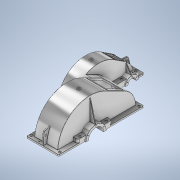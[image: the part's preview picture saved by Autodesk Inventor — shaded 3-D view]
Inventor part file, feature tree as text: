
AUTODESK INVENTOR PART (.ipt)
format: ipt  version: 2020 (Build 240168000, 168)  size: 2,549,760 bytes
history: native  units: mm
features: sketch x87, extrude x70, projected_geometry x45, plane x34, other x25, hole x17, mirror x14, fillet x14, reference x7
ambient origin geometry x8: Origin, YZ Plane, XZ Plane, XY Plane, X Axis, Y Axis, Z Axis, Center Point
bodies: 实体1 (feature_tree), 实体2 (feature_tree)
feature tree (313):
  plane  "工作平面1"
  extrude  "拉伸1"  Depth=10.0mm TaperAngle=0.0deg
  plane  "工作平面2"
  extrude  "拉伸2"  Depth=10.0mm TaperAngle=0.0deg
  plane  "工作平面3"
  extrude  "拉伸3"  Depth=10.0mm TaperAngle=0.0deg
  plane  "工作平面4"
  extrude  "拉伸4"  Depth=15.0mm TaperAngle=0.0deg
  plane  "工作平面5"
  extrude  "拉伸5"  [1 undecoded]
  sketch  "草图7"  dims[d52=10.0mm d53=0.0mm d54=10.0mm d55=0.0mm]
  plane  "工作平面6"
  extrude  "拉伸6"  Depth=10.0mm
  plane  "工作平面7"
  extrude  "拉伸7"  Depth=15.0mm
  extrude  "拉伸8"  Depth=10.0mm TaperAngle=0.0deg
  plane  "工作平面8"
  sketch  "草图11"  dims[d56=8.0mm d57=0.0mm d58=15.0mm d59=0.0mm]
  sketch  "草图12"  dims[d60=15.0mm d61=0.0mm d62=-10.0mm]
  extrude  "拉伸9"  [1 undecoded]
  extrude  "拉伸10"  Depth=10.0mm
  other  "对称面1"
  mirror  "镜像1"
  extrude  "拉伸11"  Depth=10.0mm TaperAngle=0.0deg
  sketch  "草图15"  dims[d74=15.0mm d75=0.0mm d76=10.0mm d77=0.0mm]
  other  "工作面101"
  sketch  "草图16"  dims[d78=10.0mm d79=0.0mm d80=-10.0mm]
  plane  "工作平面11"
  extrude  "拉伸12"  Depth=143.0mm TaperAngle=0.0deg
  other  "对称面2"
  extrude  "拉伸13"  Depth=10.0mm TaperAngle=0.0deg
  extrude  "拉伸14"  Depth=10.0mm TaperAngle=0.0deg
  fillet  "圆角2"  Radius=10.0mm
  extrude  "拉伸15"  Depth=10.0mm TaperAngle=0.0deg
  extrude  "拉伸16"  Depth=36.0mm
  mirror  "镜像2"
  extrude  "拉伸17"  Depth=35.0mm
  plane  "工作平面13"
  extrude  "拉伸18"  Depth=10.0mm TaperAngle=0.0deg
  plane  "工作平面14"
  extrude  "拉伸19"  Depth=10.0mm TaperAngle=0.0deg
  plane  "工作平面15"
  extrude  "拉伸20"  Depth=10.0mm TaperAngle=0.0deg
  other  "合并1"
  extrude  "拉伸21"  Depth=8.0mm TaperAngle=0.0deg
  mirror  "镜像3"
  extrude  "拉伸22"  Depth=5.0mm TaperAngle=0.0deg
  mirror  "镜像4"
  plane  "工作平面16"
  extrude  "拉伸23"  Depth=5.0mm TaperAngle=0.0deg
  extrude  "拉伸24"  Depth=36.0mm
  extrude  "拉伸25"  Depth=50.0mm
  sketch  "草图34"  dims[d131=5.0mm d132=0.0mm d133=5.0mm d134=0.0mm]
  extrude  "拉伸26"  Depth=7.0mm TaperAngle=0.0deg
  extrude  "拉伸27"  Depth=10.0mm TaperAngle=0.0deg
  sketch  "草图36"  dims[d138=5.0mm d139=0.0mm d140=50.0mm]
  extrude  "拉伸28"  Depth=70.0mm
  extrude  "拉伸29"  Depth=15.0mm TaperAngle=0.0deg
  extrude  "拉伸30"  Depth=23.0mm
  extrude  "拉伸31"  Depth=10.0mm TaperAngle=0.0deg
  extrude  "拉伸32"  Depth=36.0mm
  extrude  "拉伸33"  Depth=10.0mm TaperAngle=0.0deg
  extrude  "拉伸34"  Depth=10.0mm TaperAngle=0.0deg
  extrude  "拉伸35"  Depth=46.0mm TaperAngle=0.0deg
  extrude  "拉伸36"  Depth=12.0mm
  extrude  "拉伸37"  Depth=100.0mm
  other  "对称面4"
  mirror  "镜像5"
  extrude  "拉伸38"  Depth=46.0mm TaperAngle=0.0deg
  sketch  "草图48"  dims[d178=20.0mm d179=100.0mm]
  extrude  "拉伸39"  Depth=10.0mm TaperAngle=0.0deg
  extrude  "拉伸40"  Depth=10.0mm TaperAngle=0.0deg
  extrude  "拉伸41"  Depth=10.0mm
  extrude  "拉伸42"  [1 undecoded]
  extrude  "拉伸43"  [1 undecoded]
  extrude  "拉伸44"  Depth=10.0mm TaperAngle=0.0deg
  sketch  "草图53"  dims[d193=10.0mm d194=0.0mm d195=-10.0mm]
  extrude  "拉伸45"  Depth=113.0mm
  extrude  "拉伸46"  TaperAngle=0.0deg  [1 undecoded]
  extrude  "拉伸47"  Depth=206.0mm
  extrude  "拉伸48"  TaperAngle=0.0deg  [1 undecoded]
  extrude  "拉伸49"  Depth=1.0mm
  extrude  "拉伸50"  Depth=1.0mm
  other  "工作轴2"
  extrude  "拉伸51"  Depth=1.0mm
  plane  "工作平面19"
  mirror  "镜像6"
  plane  "工作平面20"
  mirror  "镜像7"
  fillet  "圆角3"  Radius=16.580628mm
  fillet  "圆角4"  Radius=19.198622mm
  sketch  "草图60"  dims[d213=180.0mm d214=0.0mm]
  extrude  "拉伸52"  Depth=1.0mm
  extrude  "拉伸53"  Depth=20.0mm
  extrude  "拉伸54"  TaperAngle=105.0deg  [1 undecoded]
  extrude  "拉伸55"  Depth=110.0mm
  extrude  "拉伸56"  Depth=20.0mm
  extrude  "拉伸57"  Depth=90.0mm
  plane  "工作平面21"
  plane  "工作平面22"
  extrude  "拉伸58"  Depth=90.0mm
  extrude  "拉伸59"  Depth=140.0mm
  extrude  "拉伸60"  Depth=4.0mm TaperAngle=0.0deg
  extrude  "拉伸61"  Depth=110.0mm
  extrude  "拉伸63"  [1 undecoded]
  plane  "工作平面23"
  plane  "工作平面24"
  plane  "工作平面25"
  other  "加强筋1"
  mirror  "镜像8"
  other  "加强筋2"
  other  "加强筋3"
  mirror  "镜像9"
  sketch  "草图77"  dims[d291=120.0mm d292=90.0mm]
  other  "加强筋5"
  fillet  "圆角6"  Radius=30.0mm
  hole  "孔2"  [1 undecoded]
  other  "第一对称面"
  sketch  "草图79"  dims[d293=130.0mm d294=140.0mm]
  other  "加强筋6"
  hole  "孔3"  [1 undecoded]
  fillet  "圆角7"  Radius=20.0mm
  other  "第二对称面"
  plane  "工作平面28"
  plane  "工作平面29"
  plane  "工作平面30"
  hole  "孔4"  [1 undecoded]
  sketch  "草图82"  dims[d316=18.0mm d317=110.0mm]
  extrude  "拉伸65"  Depth=170.0mm
  hole  "孔6"  [1 undecoded]
  plane  "工作平面32"
  extrude  "拉伸66"  Depth=100.0mm
  hole  "孔7"  [1 undecoded]
  plane  "工作平面34"
  extrude  "拉伸67"  Depth=6.0mm
  hole  "孔8"  [1 undecoded]
  extrude  "拉伸68"  Depth=35.0mm
  hole  "孔9"  [1 undecoded]
  mirror  "镜像10"
  hole  "孔10"  [1 undecoded]
  extrude  "拉伸69"  Depth=105.0mm
  extrude  "拉伸70"  TaperAngle=30.0deg  [1 undecoded]
  fillet  "圆角8"  Radius=28.0mm
  fillet  "圆角9"  Radius=28.0mm
  hole  "孔11"  [1 undecoded]
  hole  "孔12"  [1 undecoded]
  extrude  "拉伸71"  Depth=12.0mm
  extrude  "拉伸72"  Depth=2.0mm
  hole  "孔13"  [1 undecoded]
  plane  "工作平面35"
  mirror  "镜像11"
  plane  "工作平面36"
  hole  "孔14"  [1 undecoded]
  hole  "孔15"  [1 undecoded]
  mirror  "镜像12"
  hole  "孔16"  [1 undecoded]
  other  "工作轴3"
  other  "工作轴4"
  other  "工作轴5"
  plane  "工作平面39"
  sketch  "草图104"  dims[d410=60.0mm d412=360.0deg]
  hole  "孔17"  [1 undecoded]
  mirror  "镜像13"
  plane  "工作平面40"
  hole  "孔18"  [1 undecoded]
  mirror  "镜像14"
  plane  "工作平面41"
  hole  "孔19"  [1 undecoded]
  fillet  "圆角10"  Radius=0.15mm
  fillet  "圆角11"  Radius=0.25mm
  fillet  "圆角12"  Radius=0.375mm
  fillet  "圆角13"  Radius=14.3117mm
  fillet  "圆角14"  [1 undecoded]
  fillet  "圆角15"  [1 undecoded]
  fillet  "圆角16"  [1 undecoded]
  sketch  "草图2"  dims[d0=41.0mm d1=40.0mm d2=41.0mm d3=8.0mm d4=41.0mm d5=41.0mm d6=40.0mm d7=8.0mm d8=25.0mm d9=71.0mm d10=8.0mm d11=70.0mm d12=190.0mm d13=75.0mm d14=43.0mm d15=8.0mm d16=75.0mm d17=40.0mm d18=31.0mm d19=12.0mm d20=25.0mm d21=10.0mm d22=8.0mm d23=30.0mm d24=5.0mm d25=25.0mm d26=174.0mm d27=91.0mm d28=40.0mm d29=21.0mm d30=71.0mm d31=12.0mm d32=30.0mm d33=30.0mm d34=25.0mm d35=12.0mm d36=30.0mm d37=30.0mm d38=100.0mm d39=40.0mm d40=12.0mm d41=20.0mm d42=70.0mm d43=15.0mm d44=2.0mm d45=31.0mm d46=10.0mm d47=0.0mm]
  sketch  "草图6"  dims[d48=10.0mm d49=0.0mm d50=10.0mm d51=0.0mm]
  projected_geometry  "投影回路1"
  sketch  "草图13"  dims[d66=130.0mm d71=10.0mm]
  projected_geometry  "投影回路2"
  sketch  "草图14"  dims[d72=150.0mm d73=15.0mm]
  sketch  "草图17"  dims[d82=10.0mm d83=10.0mm]
  projected_geometry  "投影回路3"
  projected_geometry  "投影回路4"
  sketch  "草图18"  dims[d84=-10.0mm d85=10.0mm d86=0.0mm]
  projected_geometry  "投影回路5"
  sketch  "草图19"  dims[d87=10.0mm d88=0.0mm d90=143.0mm d91=0.0mm]
  projected_geometry  "投影回路6"
  sketch  "草图22"  dims[d92=6.0mm d93=10.0mm d94=0.0mm]
  sketch  "草图24"  dims[d95=10.0mm d96=0.0mm d97=10.0mm d98=0.0mm d99=10.0mm d100=0.0mm]
  sketch  "草图25"  dims[d101=10.0mm d102=0.0mm d103=10.0mm d104=0.0mm]
  sketch  "草图26"  dims[d105=10.0mm d106=0.0mm d107=36.0mm]
  projected_geometry  "投影回路7"
  projected_geometry  "投影回路8"
  sketch  "草图27"  dims[d108=10.0mm d109=0.0mm d110=35.0mm]
  sketch  "草图28"  dims[d111=10.0mm d112=0.0mm d113=10.0mm d114=0.0mm]
  projected_geometry  "投影回路9"
  sketch  "草图29"  dims[d115=10.0mm d116=0.0mm d117=10.0mm d118=0.0mm]
  sketch  "草图31"  dims[d119=10.0mm d120=0.0mm d121=10.0mm d122=0.0mm]
  projected_geometry  "投影回路11"
  sketch  "草图32"  dims[d123=8.0mm d124=0.0mm d125=8.0mm d126=0.0mm]
  projected_geometry  "投影回路12"
  sketch  "草图33"  dims[d127=5.0mm d128=0.0mm d129=5.0mm d130=0.0mm]
  projected_geometry  "投影回路13"
  projected_geometry  "投影回路14"
  sketch  "草图35"  dims[d135=5.0mm d136=0.0mm d137=36.0mm]
  projected_geometry  "投影回路15"
  sketch  "草图37"  dims[d141=5.0mm d142=0.0mm d143=7.0mm d144=0.0mm]
  projected_geometry  "投影回路16"
  sketch  "草图38"  dims[d145=10.0mm d146=0.0mm d147=10.0mm d148=0.0mm]
  projected_geometry  "投影回路17"
  sketch  "草图39"  dims[d149=10.0mm d150=0.0mm d151=70.0mm]
  projected_geometry  "投影回路18"
  sketch  "草图40"  dims[d152=10.0mm d153=0.0mm d154=15.0mm d155=0.0mm]
  projected_geometry  "投影回路19"
  sketch  "草图41"  dims[d156=23.0mm d157=0.0mm d158=23.0mm]
  projected_geometry  "投影回路20"
  projected_geometry  "投影回路21"
  sketch  "草图42"  dims[d159=36.0mm d160=10.0mm d161=0.0mm]
  projected_geometry  "投影回路22"
  sketch  "草图43"  dims[d162=23.0mm d163=36.0mm]
  projected_geometry  "投影回路23"
  sketch  "草图44"  dims[d164=10.0mm d165=0.0mm d166=10.0mm d167=0.0mm]
  sketch  "草图45"  dims[d168=10.0mm d169=0.0mm d170=10.0mm d171=0.0mm]
  sketch  "草图46"  dims[d172=70.0mm d173=46.0mm d174=0.0mm]
  sketch  "草图47"  dims[d175=10.0mm d176=0.0mm d177=12.0mm]
  projected_geometry  "投影回路24"
  sketch  "草图49"  dims[d180=46.0mm d181=0.0mm d182=46.0mm d183=0.0mm]
  projected_geometry  "投影回路25"
  sketch  "草图50"  dims[d184=380.0mm d185=10.0mm d186=0.0mm]
  sketch  "草图51"  dims[d187=390.0mm d188=10.0mm d189=0.0mm]
  projected_geometry  "投影回路26"
  sketch  "草图52"  dims[d190=10.0mm d191=0.0mm d192=10.0mm]
  projected_geometry  "投影回路27"
  sketch  "草图54"  dims[d196=10.0mm d197=-10.0mm]
  projected_geometry  "投影回路28"
  sketch  "草图55"  dims[d198=10.0mm d199=0.0mm d200=10.0mm d201=0.0mm]
  projected_geometry  "投影回路29"
  sketch  "草图56"  dims[d202=10.0mm d203=0.0mm d204=113.0mm]
  projected_geometry  "投影回路30"
  sketch  "草图57"  dims[d205=120.0mm d206=0.0mm]
  sketch  "草图58"  dims[d207=2.0mm d208=0.0mm d212=206.0mm]
  projected_geometry  "投影回路31"
  projected_geometry  "投影回路42"
  projected_geometry  "投影回路43"
  sketch  "草图61"  dims[d215=2.0mm d216=0.0mm d220=1.0mm]
  sketch  "草图62"  dims[d221=9.0mm d222=0.0mm d223=0.0mm d224=1.0mm d225=1.0mm d226=1.0mm]
  sketch  "草图63"  dims[d227=9.0mm d228=0.0mm d229=0.0mm d230=1.0mm d231=1.0mm d232=1.0mm]
  sketch  "草图64"  dims[d233=9.0mm d234=0.0mm d235=0.0mm d236=1.0mm d237=1.0mm d255=16.580628mm d256=19.198622mm]
  projected_geometry  "投影回路44"
  projected_geometry  "投影回路45"
  projected_geometry  "投影回路46"
  projected_geometry  "投影回路47"
  sketch  "草图65"  dims[d257=115.0mm d258=1.0mm]
  sketch  "草图66"  dims[d259=12.0mm d260=0.0mm d261=0.0mm d262=1.0mm d263=1.0mm d264=20.0mm]
  sketch  "草图67"  dims[d265=20.0mm d266=6.0mm d267=45.0mm d268=2.0mm d269=90.0deg d270=8.0mm d271=20.594885mm d272=105.0deg]
  projected_geometry  "投影回路48"
  sketch  "草图68"  dims[d273=19.198622mm d274=110.0mm]
  sketch  "草图70"  dims[d275=1.0mm]
  sketch  "草图72"  dims[d276=12.0mm d277=0.0mm d278=0.0mm d279=1.0mm d280=1.0mm]
  sketch  "草图73"  dims[d281=20.0mm d282=6.0mm d283=26.0mm d284=2.0mm d285=90.0deg d286=8.0mm d287=20.594885mm d288=20.0mm]
  sketch  "草图74"  dims[d289=70.0mm d290=90.0mm]
  projected_geometry  "投影回路52"
  projected_geometry  "投影回路53"
  projected_geometry  "投影回路54"
  sketch  "草图81"  dims[d295=13.5mm d296=6.0mm d297=26.0mm d298=2.0mm d299=90.0deg d300=8.0mm d301=20.594885mm d302=4.0mm d303=0.0mm]
  sketch  "草图83"  dims[d318=10.0mm d319=6.0mm d320=26.0mm d321=2.0mm d322=90.0deg d323=8.0mm d324=20.594885mm d325=-3.0mm d326=30.0mm]
  sketch  "草图85"  dims[d327=10.0mm d328=0.0mm]
  plane  "工作平面31"
  sketch  "草图86"  dims[d329=15.29367mm d330=36.0mm d331=18.0mm d332=2.0mm d333=90.0deg d334=47.2mm d335=0.0mm d336=-3.0mm]
  sketch  "草图87"  dims[d337=30.0mm d338=10.0mm d339=0.0mm]
  plane  "工作平面33"
  sketch  "草图88"  dims[d340=15.29367mm d341=36.0mm d342=18.0mm d343=2.0mm d344=90.0deg d345=47.2mm d346=0.0mm d347=20.0mm d348=0.0mm]
  sketch  "草图89"  dims[d349=36.001mm d350=70.0mm]
  sketch  "草图90"  dims[d351=13.5mm d352=36.0mm d353=26.0mm d354=2.0mm d355=90.0deg d356=8.0mm d357=0.0mm]
  projected_geometry  "投影回路56"
  sketch  "草图91"  dims[d358=13.5mm d359=6.0mm d360=26.0mm d361=2.0mm d362=90.0deg d363=8.0mm d364=0.0mm d365=170.0mm]
  sketch  "草图92"  dims[d366=150.0mm d367=15.0mm]
  reference  "参考1"
  reference  "参考2"
  reference  "参考3"
  reference  "参考4"
  reference  "参考5"
  sketch  "草图93"  dims[d368=4.0mm d369=0.0mm d370=100.0mm]
  sketch  "草图94"  dims[d371=80.0mm d372=10.0mm]
  sketch  "草图95"  dims[d373=10.0mm d374=0.0mm d375=6.0mm]
  sketch  "草图96"  dims[d376=6.0mm]
  sketch  "草图97"  dims[d377=4.917mm d378=12.0mm d379=26.0mm d380=2.0mm d381=90.0deg d382=17.1mm d383=0.0mm]
  sketch  "草图98"  dims[d384=4.917mm d385=12.0mm d386=26.0mm d387=2.0mm d388=90.0deg d389=17.1mm d390=0.0mm d391=35.0mm]
  sketch  "草图100"  dims[d392=2.0mm d393=0.0mm d394=35.0mm]
  sketch  "草图101"  dims[d395=2.0mm d396=0.0mm d397=175.0mm]
  sketch  "草图102"  dims[d398=60.0mm d400=360.0deg]
  sketch  "草图103"  dims[d402=8.376mm d403=15.0mm d404=4.0mm d405=2.0mm d406=90.0deg d407=18.0mm d408=20.594885mm d409=165.0mm]
  reference  "参考8"
  projected_geometry  "投影回路57"
  plane  "工作平面37"
  plane  "工作平面38"
  reference  "参考9"
  projected_geometry  "投影回路58"
  sketch  "草图105"  dims[d414=8.376mm d415=15.0mm d416=4.0mm d417=2.0mm d418=90.0deg d419=18.0mm d420=20.594885mm d421=105.0mm]
  sketch  "草图106"  dims[d422=60.0mm d424=360.0deg]
  projected_geometry  "投影回路59"
  sketch  "草图107"  dims[d426=8.376mm d427=15.0mm d428=4.0mm d429=2.0mm d430=90.0deg d431=18.0mm d432=20.594885mm d433=8.376mm d434=15.0mm d435=4.0mm d436=2.0mm d437=90.0deg d438=18.0mm d439=20.594885mm d440=30.0deg d441=28.0mm d442=6.647mm d443=16.0mm d444=4.0mm d445=2.0mm d446=90.0deg d447=22.2mm d448=20.594885mm d449=28.0mm d450=6.647mm d451=16.0mm d452=4.0mm d453=2.0mm d454=90.0deg d455=22.2mm d456=20.594885mm d457=28.0mm d458=6.647mm d459=16.0mm d460=4.0mm d461=2.0mm d462=90.0deg d463=22.2mm d464=20.594885mm d465=20.0mm d466=12.0mm d467=2.0mm d468=1.0mm d469=2.0mm d470=2.0mm d471=2.0mm d248=1.0mm d249=1.0mm d250=1.0mm d251=0.15mm d252=0.25mm d253=0.375mm d254=14.3117mm]
  projected_geometry  "投影回路60"
  other  "<userpath>\Desktop\ME_course_project\课设试试\shaft_try_1.iam"
  other  "shaft_try_1.iam"
  other  "低速级"
  other  "正齿轮2:1"
  other  "xia(1):1"
  other  "<userpath>\Desktop\111111\Workspace\cpz assemble.iam"
  other  "cpz assemble.iam"
  other  "轴承通盖:1"
  other  "轴承通盖1:1"
note: 29 required parameter values undecoded (feature->parameter linkage not recoverable at this tier; creation-order binding heuristic only, values carry confidence <= 0.55)
